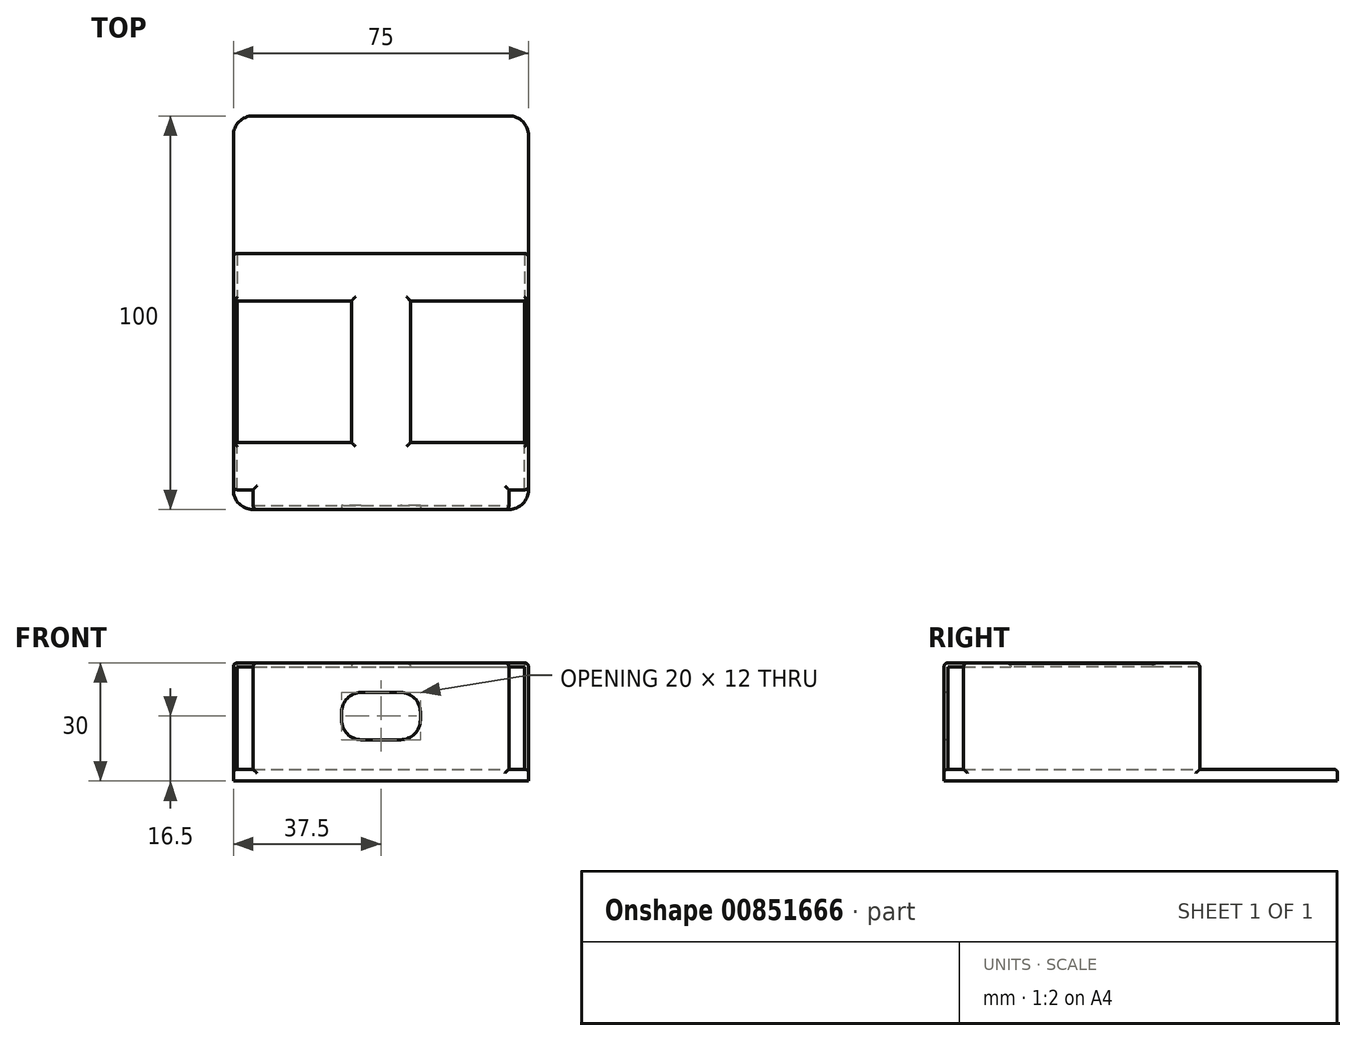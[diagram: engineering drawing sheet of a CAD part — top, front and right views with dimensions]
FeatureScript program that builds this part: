
annotation { "Feature Type Name" : "Feature", "Feature Type Description" : "" }
export const myFeature = defineFeature(function(context is Context, id is Id, definition is map)
    precondition{}
    {
        {
            var Q0;
            Q0=qCreatedBy(makeId("Top.planeOp"),FACE);
            var sketch = newSketch(context, id + "F0", { "sketchPlane" : qUnion([Q0])});
            skLineSegment(sketch, "E0.bottom", {"start": v(5, 0) * mm, "end": v(70, 0) * mm});
            skLineSegment(sketch, "E0.top", {"start": v(5, 100) * mm, "end": v(70, 100) * mm});
            skLineSegment(sketch, "E0.left", {"start": v(0, 5) * mm, "end": v(0, 95) * mm});
            skLineSegment(sketch, "E0.right", {"start": v(75, 5) * mm, "end": v(75, 95) * mm});
            skPoint(sketch, "E1.visualSharp", {"position": v(0, 100) * mm});
            skArc(sketch, "E1.filletArc", {"start": v(5, 100) * mm, "mid": v(1.46, 98.54) * mm, "end": v(0, 95) * mm});
            skPoint(sketch, "E2.visualSharp", {"position": v(75, 100) * mm});
            skArc(sketch, "E2.filletArc", {"start": v(75, 95) * mm, "mid": v(73.54, 98.54) * mm, "end": v(70, 100) * mm});
            skPoint(sketch, "E3.visualSharp", {"position": v(75, 0) * mm});
            skArc(sketch, "E3.filletArc", {"start": v(70, 0) * mm, "mid": v(73.54, 1.46) * mm, "end": v(75, 5) * mm});
            skPoint(sketch, "E4.visualSharp", {"position": v(0, 0) * mm});
            skArc(sketch, "E4.filletArc", {"start": v(0, 5) * mm, "mid": v(1.46, 1.46) * mm, "end": v(5, 0) * mm});
            skSolve(sketch);
        }
        {
            var Q0;
            Q0=makeQuery(id+"F0.imprint","IMPRINT",FACE,{"disambiguationData":[TD([[makeQuery(id+"F0.imprint","IMPRINT",EDGE,{"derivedFrom":sQuery(id+"F0.wireOp",EDGE,"E0.bottom")}),1.0]])]});
            extrude(context, id + "F1", {"entities" : qUnion([Q0]), "depth" : 3 * mm, "offsetDistance" : 25 * mm});
        }
        {
            var Q0;
            Q0=makeQuery(id+"F1.opExtrude","CAP_FACE",FACE,{"disambiguationData":[OSD([sQuery(id+"F0.wireOp",EDGE,"E0.bottom"),sQuery(id+"F0.wireOp",EDGE,"E0.top"),sQuery(id+"F0.wireOp",EDGE,"E0.left"),sQuery(id+"F0.wireOp",EDGE,"E0.right"),sQuery(id+"F0.wireOp",EDGE,"E1.filletArc"),sQuery(id+"F0.wireOp",EDGE,"E2.filletArc"),sQuery(id+"F0.wireOp",EDGE,"E3.filletArc"),sQuery(id+"F0.wireOp",EDGE,"E4.filletArc")])],"isStart":false});
            var sketch = newSketch(context, id + "F2", { "sketchPlane" : qUnion([Q0])});
            skPoint(sketch, "E5.oppositeSnap0", {"position": v(77.54, 1) * mm});
            skLineSegment(sketch, "E5.bottom", {"start": v(5, 0) * mm, "end": v(70, 0) * mm});
            skLineSegment(sketch, "E5.top", {"start": v(5, 1) * mm, "end": v(70, 1) * mm});
            skLineSegment(sketch, "E5.left", {"start": v(5, 0) * mm, "end": v(5, 1) * mm});
            skLineSegment(sketch, "E5.right", {"start": v(70, 0) * mm, "end": v(70, 1) * mm});
            skPoint(sketch, "E6.oppositeSnap0", {"position": v(1.46, 1.46) * mm});
            skLineSegment(sketch, "E7.bottom", {"start": v(0, 5) * mm, "end": v(1, 5) * mm});
            skLineSegment(sketch, "E7.top", {"start": v(0, 65) * mm, "end": v(1, 65) * mm});
            skLineSegment(sketch, "E7.left", {"start": v(0, 5) * mm, "end": v(0, 65) * mm});
            skLineSegment(sketch, "E7.right", {"start": v(1, 5) * mm, "end": v(1, 65) * mm});
            skLineSegment(sketch, "E8.bottom", {"start": v(75, 5) * mm, "end": v(74, 5) * mm});
            skLineSegment(sketch, "E8.top", {"start": v(75, 65) * mm, "end": v(74, 65) * mm});
            skLineSegment(sketch, "E8.left", {"start": v(75, 5) * mm, "end": v(75, 65) * mm});
            skLineSegment(sketch, "E8.right", {"start": v(74, 5) * mm, "end": v(74, 65) * mm});
            skSolve(sketch);
        }
        {
            var Q0;
            Q0=makeQuery(id+"F2.imprint","IMPRINT",FACE,{"disambiguationData":[TD([[makeQuery(id+"F2.imprint","IMPRINT",EDGE,{"derivedFrom":sQuery(id+"F2.wireOp",EDGE,"E7.bottom")}),1.0]])]});
            var Q1;
            Q1=makeQuery(id+"F2.imprint","IMPRINT",FACE,{"disambiguationData":[TD([[makeQuery(id+"F2.imprint","IMPRINT",EDGE,{"derivedFrom":sQuery(id+"F2.wireOp",EDGE,"E5.bottom")}),1.0]])]});
            var Q2;
            Q2=makeQuery(id+"F2.imprint","IMPRINT",FACE,{"disambiguationData":[TD([[makeQuery(id+"F2.imprint","IMPRINT",EDGE,{"derivedFrom":sQuery(id+"F2.wireOp",EDGE,"E8.bottom")}),-1.0]])]});
            extrude(context, id + "F3", {"entities" : qUnion([Q0, Q1, Q2]), "operationType" : NewBodyOperationType.ADD, "depth" : 27 * mm, "offsetDistance" : 25 * mm});
        }
        {
            var Q0;
            Q0=makeQuery(id+"F3.opExtrude","SWEPT_FACE",FACE,{"disambiguationData":[OSD([sQuery(id+"F2.wireOp",EDGE,"E8.right")])]});
            var sketch = newSketch(context, id + "F4", { "sketchPlane" : qUnion([Q0])});
            skLineSegment(sketch, "E9.bottom", {"start": v(-5, 30) * mm, "end": v(-17, 30) * mm});
            skLineSegment(sketch, "E9.top", {"start": v(-5, 29) * mm, "end": v(-17, 29) * mm});
            skLineSegment(sketch, "E9.left", {"start": v(-5, 30) * mm, "end": v(-5, 29) * mm});
            skLineSegment(sketch, "E9.right", {"start": v(-17, 30) * mm, "end": v(-17, 29) * mm});
            skLineSegment(sketch, "E10.bottom", {"start": v(-65, 30) * mm, "end": v(-53, 30) * mm});
            skLineSegment(sketch, "E10.top", {"start": v(-65, 29) * mm, "end": v(-53, 29) * mm});
            skLineSegment(sketch, "E10.left", {"start": v(-65, 30) * mm, "end": v(-65, 29) * mm});
            skLineSegment(sketch, "E10.right", {"start": v(-53, 30) * mm, "end": v(-53, 29) * mm});
            skSolve(sketch);
        }
        {
            var Q0;
            Q0 = qSketchRegion(id + "F4", true);
            extrude(context, id + "F5", {"entities" : qUnion([Q0]), "operationType" : NewBodyOperationType.ADD, "endBound" : BoundingType.UP_TO_NEXT, "depth" : 25 * mm, "offsetDistance" : 25 * mm});
        }
        {
            var Q0;
            Q0=makeQuery(id+"F3.opExtrude","SWEPT_FACE",FACE,{"disambiguationData":[OSD([sQuery(id+"F2.wireOp",EDGE,"E5.top")])]});
            var sketch = newSketch(context, id + "F6", { "sketchPlane" : qUnion([Q0])});
            skLineSegment(sketch, "E11.bottom", {"start": v(-5, 30) * mm, "end": v(-70, 30) * mm});
            skLineSegment(sketch, "E11.top", {"start": v(-5, 29) * mm, "end": v(-70, 29) * mm});
            skLineSegment(sketch, "E11.left", {"start": v(-5, 30) * mm, "end": v(-5, 29) * mm});
            skLineSegment(sketch, "E11.right", {"start": v(-70, 30) * mm, "end": v(-70, 29) * mm});
            skSolve(sketch);
        }
        {
            var Q0;
            Q0 = qSketchRegion(id + "F6", true);
            extrude(context, id + "F7", {"entities" : qUnion([Q0]), "operationType" : NewBodyOperationType.ADD, "endBound" : BoundingType.UP_TO_NEXT, "depth" : 25 * mm, "offsetDistance" : 25 * mm});
        }
        {
            var Q0;
            Q0=makeQuery(id+"F5.opExtrude","SWEPT_FACE",FACE,{"disambiguationData":[OSD([sQuery(id+"F4.wireOp",EDGE,"E9.right")])]});
            var sketch = newSketch(context, id + "F8", { "sketchPlane" : qUnion([Q0])});
            skLineSegment(sketch, "E12.bottom", {"start": v(-30, 30) * mm, "end": v(-45, 30) * mm});
            skLineSegment(sketch, "E12.top", {"start": v(-30, 29) * mm, "end": v(-45, 29) * mm});
            skLineSegment(sketch, "E12.left", {"start": v(-30, 30) * mm, "end": v(-30, 29) * mm});
            skLineSegment(sketch, "E12.right", {"start": v(-45, 30) * mm, "end": v(-45, 29) * mm});
            skPoint(sketch, "E13", {"position": v(-37.5, 30) * mm});
            skSolve(sketch);
        }
        {
            var Q0;
            Q0 = qSketchRegion(id + "F8", true);
            extrude(context, id + "F9", {"entities" : qUnion([Q0]), "operationType" : NewBodyOperationType.ADD, "endBound" : BoundingType.UP_TO_NEXT, "depth" : 25 * mm, "offsetDistance" : 25 * mm});
        }
        {
            var Q0;
            Q0=makeQuery(id+"F3.boolean.opBoolean","MERGE",FACE,{"derivedFrom":[makeQuery(id+"F1.opExtrude","SWEPT_FACE",FACE,{"disambiguationData":[OSD([sQuery(id+"F0.wireOp",EDGE,"E0.bottom")])]}),makeQuery(id+"F3.opExtrude","SWEPT_FACE",FACE,{"disambiguationData":[OSD([sQuery(id+"F2.wireOp",EDGE,"E5.bottom")])]})]});
            var sketch = newSketch(context, id + "F10", { "sketchPlane" : qUnion([Q0])});
            skLineSegment(sketch, "E14.bottom", {"start": v(42.5, 22.5) * mm, "end": v(32.5, 22.5) * mm});
            skLineSegment(sketch, "E14.top", {"start": v(42.5, 10.5) * mm, "end": v(32.5, 10.5) * mm});
            skLineSegment(sketch, "E14.left", {"start": v(47.5, 17.5) * mm, "end": v(47.5, 15.5) * mm});
            skLineSegment(sketch, "E14.right", {"start": v(27.5, 17.5) * mm, "end": v(27.5, 15.5) * mm});
            skLineSegment(sketch, "E15", {"start": v(47.5, 16.5) * mm, "end": v(70, 16.5) * mm, "construction": true});
            skLineSegment(sketch, "E16", {"start": v(27.5, 16.5) * mm, "end": v(5, 16.5) * mm, "construction": true});
            skPoint(sketch, "E17.visualSharp", {"position": v(47.5, 22.5) * mm});
            skArc(sketch, "E17.filletArc", {"start": v(47.5, 17.5) * mm, "mid": v(46.04, 21.04) * mm, "end": v(42.5, 22.5) * mm});
            skPoint(sketch, "E18.visualSharp", {"position": v(47.5, 10.5) * mm});
            skArc(sketch, "E18.filletArc", {"start": v(42.5, 10.5) * mm, "mid": v(46.04, 11.96) * mm, "end": v(47.5, 15.5) * mm});
            skPoint(sketch, "E19.visualSharp", {"position": v(27.5, 10.5) * mm});
            skArc(sketch, "E19.filletArc", {"start": v(27.5, 15.5) * mm, "mid": v(28.96, 11.96) * mm, "end": v(32.5, 10.5) * mm});
            skPoint(sketch, "E20.visualSharp", {"position": v(27.5, 22.5) * mm});
            skArc(sketch, "E20.filletArc", {"start": v(32.5, 22.5) * mm, "mid": v(28.96, 21.04) * mm, "end": v(27.5, 17.5) * mm});
            skSolve(sketch);
        }
        {
            var Q0;
            Q0=makeQuery(id+"F10.imprint","IMPRINT",FACE,{"disambiguationData":[TD([[makeQuery(id+"F10.imprint","IMPRINT",EDGE,{"derivedFrom":sQuery(id+"F10.wireOp",EDGE,"E14.bottom")}),1.0]])]});
            extrude(context, id + "F11", {"entities" : qUnion([Q0]), "operationType" : NewBodyOperationType.REMOVE, "oppositeDirection" : true, "depth" : 25 * mm, "offsetDistance" : 25 * mm});
        }
        {
            var Q0;
            Q0=makeQuery(id+"F3.opExtrude","CAP_EDGE",EDGE,{"disambiguationData":[OSD([sQuery(id+"F2.wireOp",EDGE,"E8.left")])],"isStart":false});
            var Q1;
            Q1=makeQuery(id+"F3.opExtrude","CAP_EDGE",EDGE,{"disambiguationData":[OSD([sQuery(id+"F2.wireOp",EDGE,"E7.left")])],"isStart":false});
            var Q2;
            Q2=makeQuery(id+"F5.boolean.opBoolean","MERGE",EDGE,{"derivedFrom":[makeQuery(id+"F3.opExtrude","CAP_EDGE",EDGE,{"disambiguationData":[OSD([sQuery(id+"F2.wireOp",EDGE,"E7.top")])],"isStart":false}),makeQuery(id+"F3.opExtrude","CAP_EDGE",EDGE,{"disambiguationData":[OSD([sQuery(id+"F2.wireOp",EDGE,"E8.top")])],"isStart":false}),makeQuery(id+"F5.opExtrude","SWEPT_EDGE",EDGE,{"disambiguationData":[OSD([sQuery(id+"F4.wireOp",EDGE,"E10.bottom"),sQuery(id+"F4.wireOp",EDGE,"E10.left")])]})]});
            var Q3;
            Q3=makeQuery(id+"F3.opExtrude","SWEPT_EDGE",EDGE,{"disambiguationData":[OSD([sQuery(id+"F0.wireOp",EDGE,"E0.right"),sQuery(id+"F2.wireOp",EDGE,"E8.top"),sQuery(id+"F2.wireOp",EDGE,"E8.left")])]});
            var Q4;
            Q4=makeQuery(id+"F3.opExtrude","SWEPT_EDGE",EDGE,{"disambiguationData":[OSD([sQuery(id+"F0.wireOp",EDGE,"E0.left"),sQuery(id+"F2.wireOp",EDGE,"E7.top"),sQuery(id+"F2.wireOp",EDGE,"E7.left")])]});
            var Q5;
            Q5=makeQuery(id+"F1.opExtrude","CAP_EDGE",EDGE,{"disambiguationData":[OSD([sQuery(id+"F0.wireOp",EDGE,"E0.top")])],"isStart":false});
            var Q6;
            Q6=makeQuery(id+"F9.opExtrude","SWEPT_EDGE",EDGE,{"disambiguationData":[OSD([sQuery(id+"F2.wireOp",EDGE,"E8.right"),sQuery(id+"F4.wireOp",EDGE,"E9.bottom"),sQuery(id+"F4.wireOp",EDGE,"E9.right"),sQuery(id+"F8.wireOp",EDGE,"E12.bottom"),sQuery(id+"F8.wireOp",EDGE,"E12.left")])]});
            var Q7;
            {var subQ0=sQuery(id+"F2.wireOp",EDGE,"E8.right");var subQ1=sQuery(id+"F4.wireOp",EDGE,"E10.right");var subQ2=sQuery(id+"F2.wireOp",EDGE,"E7.right");var subQ3=sQuery(id+"F4.wireOp",EDGE,"E10.bottom");Q7=makeQuery(id+"F9.boolean.opBoolean","SPLIT",EDGE,{"disambiguationData":[TD([makeQuery(id+"F3.opExtrude","SWEPT_FACE",FACE,{"disambiguationData":[OSD([subQ2])]})])],"derivedFrom":makeQuery(id+"F5.opExtrude","SWEPT_EDGE",EDGE,{"disambiguationData":[OSD([subQ0,subQ3,subQ1])]})});}
            var Q8;
            Q8=makeQuery(id+"F9.opExtrude","SWEPT_EDGE",EDGE,{"disambiguationData":[OSD([sQuery(id+"F2.wireOp",EDGE,"E8.right"),sQuery(id+"F4.wireOp",EDGE,"E9.bottom"),sQuery(id+"F4.wireOp",EDGE,"E9.right"),sQuery(id+"F8.wireOp",EDGE,"E12.bottom"),sQuery(id+"F8.wireOp",EDGE,"E12.right")])]});
            var Q9;
            {var subQ0=sQuery(id+"F2.wireOp",EDGE,"E8.right");var subQ1=sQuery(id+"F4.wireOp",EDGE,"E10.right");var subQ2=sQuery(id+"F4.wireOp",EDGE,"E10.bottom");Q9=makeQuery(id+"F9.boolean.opBoolean","SPLIT",EDGE,{"disambiguationData":[TD([makeQuery(id+"F3.opExtrude","SWEPT_FACE",FACE,{"disambiguationData":[OSD([subQ0])]})])],"derivedFrom":makeQuery(id+"F5.opExtrude","SWEPT_EDGE",EDGE,{"disambiguationData":[OSD([subQ0,subQ2,subQ1])]})});}
            var Q10;
            {var subQ0=sQuery(id+"F2.wireOp",EDGE,"E8.right");var subQ1=sQuery(id+"F4.wireOp",EDGE,"E9.bottom");var subQ2=sQuery(id+"F4.wireOp",EDGE,"E9.right");Q10=makeQuery(id+"F9.boolean.opBoolean","SPLIT",EDGE,{"disambiguationData":[TD([makeQuery(id+"F3.opExtrude","SWEPT_FACE",FACE,{"disambiguationData":[OSD([subQ0])]})])],"derivedFrom":makeQuery(id+"F5.opExtrude","SWEPT_EDGE",EDGE,{"disambiguationData":[OSD([subQ0,subQ1,subQ2])]})});}
            var Q11;
            {var subQ0=sQuery(id+"F2.wireOp",EDGE,"E8.right");var subQ1=sQuery(id+"F2.wireOp",EDGE,"E7.right");var subQ2=sQuery(id+"F4.wireOp",EDGE,"E9.bottom");var subQ3=sQuery(id+"F4.wireOp",EDGE,"E9.right");Q11=makeQuery(id+"F9.boolean.opBoolean","SPLIT",EDGE,{"disambiguationData":[TD([makeQuery(id+"F3.opExtrude","SWEPT_FACE",FACE,{"disambiguationData":[OSD([subQ1])]})])],"derivedFrom":makeQuery(id+"F5.opExtrude","SWEPT_EDGE",EDGE,{"disambiguationData":[OSD([subQ0,subQ2,subQ3])]})});}
            var Q12;
            Q12=makeQuery(id+"F3.opExtrude","CAP_EDGE",EDGE,{"disambiguationData":[OSD([sQuery(id+"F2.wireOp",EDGE,"E8.right")])],"isStart":false});
            var Q13;
            Q13=makeQuery(id+"F3.opExtrude","CAP_EDGE",EDGE,{"disambiguationData":[OSD([sQuery(id+"F2.wireOp",EDGE,"E7.right")])],"isStart":false});
            var Q14;
            {var subQ1=sQuery(id+"F2.wireOp",EDGE,"E8.bottom");var subQ2=sQuery(id+"F2.wireOp",EDGE,"E7.right");var subQ3=sQuery(id+"F2.wireOp",EDGE,"E7.bottom");Q14=makeQuery(id+"F7.boolean.opBoolean","SPLIT",EDGE,{"disambiguationData":[TD([makeQuery(id+"F1.opExtrude","SWEPT_FACE",FACE,{"disambiguationData":[OSD([sQuery(id+"F0.wireOp",EDGE,"E0.right")])]})])],"derivedFrom":makeQuery(id+"F5.boolean.opBoolean","MERGE",EDGE,{"derivedFrom":[makeQuery(id+"F3.opExtrude","CAP_EDGE",EDGE,{"disambiguationData":[OSD([subQ3])],"isStart":false}),makeQuery(id+"F3.opExtrude","CAP_EDGE",EDGE,{"disambiguationData":[OSD([subQ1])],"isStart":false}),makeQuery(id+"F5.opExtrude","SWEPT_EDGE",EDGE,{"disambiguationData":[OSD([subQ3,subQ2])]})]})});}
            var Q15;
            Q15=makeQuery(id+"F7.boolean.opBoolean","MERGE",EDGE,{"derivedFrom":[makeQuery(id+"F3.opExtrude","CAP_EDGE",EDGE,{"disambiguationData":[OSD([sQuery(id+"F2.wireOp",EDGE,"E5.right")])],"isStart":false}),makeQuery(id+"F7.opExtrude","SWEPT_EDGE",EDGE,{"disambiguationData":[OSD([sQuery(id+"F6.wireOp",EDGE,"E11.bottom"),sQuery(id+"F6.wireOp",EDGE,"E11.right")])]})]});
            var Q16;
            Q16=makeQuery(id+"F7.boolean.opBoolean","MERGE",EDGE,{"derivedFrom":[makeQuery(id+"F3.opExtrude","CAP_EDGE",EDGE,{"disambiguationData":[OSD([sQuery(id+"F2.wireOp",EDGE,"E5.left")])],"isStart":false}),makeQuery(id+"F7.opExtrude","SWEPT_EDGE",EDGE,{"disambiguationData":[OSD([sQuery(id+"F6.wireOp",EDGE,"E11.bottom"),sQuery(id+"F6.wireOp",EDGE,"E11.left")])]})]});
            var Q17;
            {var subQ0=sQuery(id+"F2.wireOp",EDGE,"E8.bottom");var subQ2=sQuery(id+"F2.wireOp",EDGE,"E7.right");var subQ3=sQuery(id+"F2.wireOp",EDGE,"E7.bottom");Q17=makeQuery(id+"F7.boolean.opBoolean","SPLIT",EDGE,{"disambiguationData":[TD([makeQuery(id+"F1.opExtrude","SWEPT_FACE",FACE,{"disambiguationData":[OSD([sQuery(id+"F0.wireOp",EDGE,"E0.left")])]})])],"derivedFrom":makeQuery(id+"F5.boolean.opBoolean","MERGE",EDGE,{"derivedFrom":[makeQuery(id+"F3.opExtrude","CAP_EDGE",EDGE,{"disambiguationData":[OSD([subQ3])],"isStart":false}),makeQuery(id+"F3.opExtrude","CAP_EDGE",EDGE,{"disambiguationData":[OSD([subQ0])],"isStart":false}),makeQuery(id+"F5.opExtrude","SWEPT_EDGE",EDGE,{"disambiguationData":[OSD([subQ3,subQ2])]})]})});}
            var Q18;
            Q18=makeQuery(id+"F3.opExtrude","CAP_EDGE",EDGE,{"disambiguationData":[OSD([sQuery(id+"F2.wireOp",EDGE,"E5.bottom")])],"isStart":false});
            var Q19;
            Q19=makeQuery(id+"F11.boolean.opBoolean","COPY",EDGE,{"derivedFrom":makeQuery(id+"F11.opExtrude","CAP_EDGE",EDGE,{"disambiguationData":[OSD([sQuery(id+"F10.wireOp",EDGE,"E14.bottom")])],"isStart":true})});
            var Q20;
            Q20=makeQuery(id+"F11.boolean.opBoolean","COPY",EDGE,{"derivedFrom":makeQuery(id+"F11.opExtrude","CAP_EDGE",EDGE,{"disambiguationData":[OSD([sQuery(id+"F10.wireOp",EDGE,"E17.filletArc")])],"isStart":true})});
            var Q21;
            Q21=makeQuery(id+"F3.opExtrude","SWEPT_EDGE",EDGE,{"disambiguationData":[OSD([sQuery(id+"F0.wireOp",EDGE,"E4.filletArc"),sQuery(id+"F2.wireOp",EDGE,"E5.bottom"),sQuery(id+"F2.wireOp",EDGE,"E5.left")])]});
            var Q22;
            Q22=makeQuery(id+"F3.opExtrude","SWEPT_EDGE",EDGE,{"disambiguationData":[OSD([sQuery(id+"F0.wireOp",EDGE,"E4.filletArc"),sQuery(id+"F2.wireOp",EDGE,"E7.bottom"),sQuery(id+"F2.wireOp",EDGE,"E7.left")])]});
            var Q23;
            Q23=makeQuery(id+"F1.opExtrude","CAP_EDGE",EDGE,{"disambiguationData":[OSD([sQuery(id+"F0.wireOp",EDGE,"E4.filletArc")])],"isStart":false});
            var Q24;
            Q24=makeQuery(id+"F3.opExtrude","SWEPT_EDGE",EDGE,{"disambiguationData":[OSD([sQuery(id+"F0.wireOp",EDGE,"E3.filletArc"),sQuery(id+"F2.wireOp",EDGE,"E5.bottom"),sQuery(id+"F2.wireOp",EDGE,"E5.right")])]});
            var Q25;
            Q25=makeQuery(id+"F3.opExtrude","SWEPT_EDGE",EDGE,{"disambiguationData":[OSD([sQuery(id+"F0.wireOp",EDGE,"E3.filletArc"),sQuery(id+"F2.wireOp",EDGE,"E8.bottom"),sQuery(id+"F2.wireOp",EDGE,"E8.left")])]});
            var Q26;
            Q26=makeQuery(id+"F1.opExtrude","CAP_EDGE",EDGE,{"disambiguationData":[OSD([sQuery(id+"F0.wireOp",EDGE,"E3.filletArc")])],"isStart":false});
            fillet(context, id + "F12", {"entities" : qUnion([Q0, Q1, Q2, Q3, Q4, Q5, Q6, Q7, Q8, Q9, Q10, Q11, Q12, Q13, Q14, Q15, Q16, Q17, Q18, Q19, Q20, Q21, Q22, Q23, Q24, Q25, Q26]), "radius" : 1 * mm, "tangentPropagation" : true, "allowEdgeOverflow" : false});
        }
    });
